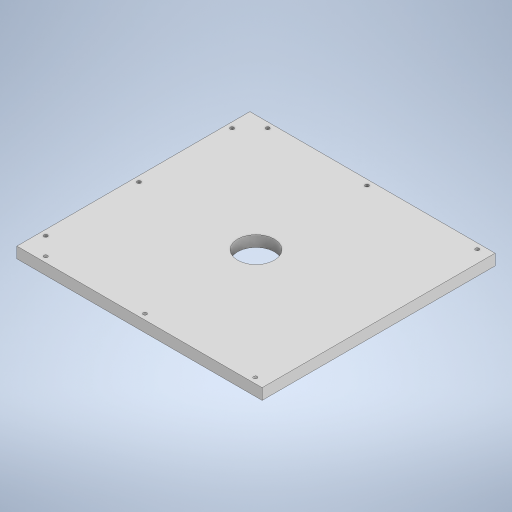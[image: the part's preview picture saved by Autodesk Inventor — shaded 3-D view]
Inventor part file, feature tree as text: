
AUTODESK INVENTOR PART (.ipt)
format: ipt  version: 2023.2 (Build 272271030, 271C)  size: 380,416 bytes
history: native  units: mm
features: extrude x4, sketch x3, projected_geometry x2
ambient origin geometry x8: Origin, YZ Plane, XZ Plane, XY Plane, X Axis, Y Axis, Z Axis, Center Point
bodies: Solid1 (feature_tree)
feature tree (9):
  extrude  "Extrusion1"  Depth=190.0mm
  extrude  "Extrusion10"  Depth=9.0mm
  sketch  "Sketch14"  dims[d28=9.0mm d29=0.0mm d47=9.0mm d48=9.0mm d49=9.0mm d50=3.0mm d51=3.0mm d52=3.0mm d53=10.0mm d54=0.0mm d55=3.0mm d56=3.0mm d57=3.0mm d58=10.0mm d59=0.0mm]
  extrude  "Extrusion14"  Depth=9.0mm
  extrude  "Extrusion15"  Depth=9.0mm
  sketch  "Sketch1"  dims[d0=200.0mm d1=190.0mm]
  sketch  "Sketch10"  dims[d2=9.0mm d3=0.0mm d27=30.0mm]
  projected_geometry  "Projected Loop8"
  projected_geometry  "Projected Loop12"
